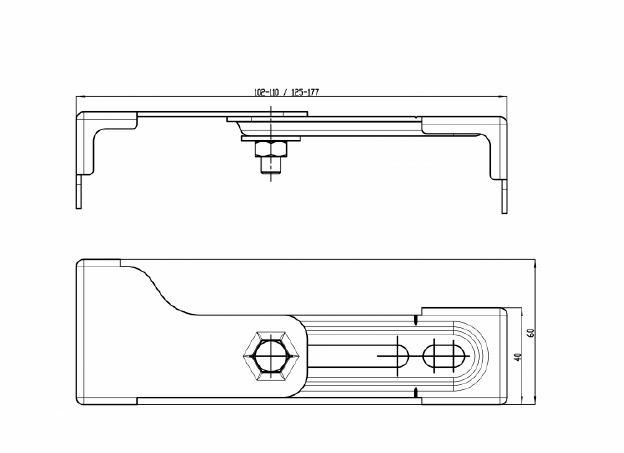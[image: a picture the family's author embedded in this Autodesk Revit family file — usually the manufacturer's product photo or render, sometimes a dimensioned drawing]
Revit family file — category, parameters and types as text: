
# Revit family: PRD_AR_PrplmbInstalFrm_InstallationFrameForToiletBowl_AQFX0006,0007
name_source: partatom
category: Plumbing Fixtures
revit_build: Autodesk Revit 2018 (Build: 20190510_1515(x64)
units: mm (PartAtom-declared; Revit-internal decimal feet)

## family parameters
Always vertical = Yes
Cut with Voids When Loaded = Yes
OmniClass Number = 23.45.00.00
OmniClass Title = Sanitary, Laundry, and Cleaning Equipment
Part Type = Normal
Room Calculation Point = No
Round Connector Dimension = Use Diameter
Shared = No
Work Plane-Based = No

## types (4) — shared parameters
Application = WC
AssetType = Fixed
Category = Pr_40_20_93_62, Pre-plumbed installation frames
Cistern = PRD_AR_PlasticMaterial
CisternCapacity = 0
CisternColor = White
CisternHeight = Other
CisternMaterial = Plastic
DurationUnit = year
Finish = powder coated
FlushRate = 0
FlushType = Push
Form = Installation frame
FrameMaterial = PRD_AR_StainlessSteel_Colored
HeightAdjustment = 200 mm  [stored 0.656168 ft]
IfcExportAs = IfcSanitaryTerminalType
IfcExportType = CISTERN
InletPipeSize = 50  [stored 0.164042 ft]
InstallationDate = 1900-12-31T23:59:59
IsAutomaticFlush = 0
IsSingleFlush = 0
Manufacturer = KWC Group AG
ManufacturerName = KWC Group AG
ManufacturerURL = www.kwc.com
Material = steel
Materials = powder coated steel
NBSDescription = Preplumbed installation frames
NBSReference = 45-35-70/421
NominalDepth = 155 mm
NominalHeight = 1120 mm  [stored 3.67454 ft]
NominalWidth = 450 mm
OverallWidth = 450 mm
ProductInformation = https://pim.kwc.com
Size = 450x1120x(135-205) mm
Type = Installation element
TypeOfMixing = no mixing
TypeOfMounting = wall and floor mounting
URL = www.kwc.com
Uniclass2015Code = Pr_40_20_93_62
Uniclass2015Title = Pre-plumbed installation frames
Uniclass2015Version = Products v1.10
Version = 1
WarrantyDurationUnit = year
WarrantyStartDate = 1900-12-31T23:59:59

## per-type parameters (varying)
| type | BIMObjectName | BarrierFree | Description | Features | GrossWeight | InletHeight | Model | ModelNumber | ModelReference | Name | NetWeight | OutletHeight | OutletPipeSize | OutletSize |
| AQFX0007 - DN100 | PRD_AR_PreplumbedInstallationFrames_InstallationFrameForToiletBowl_AQFX0007 | yes | AQUAFIX installation frame for barrier-free wall-mounted toilet bowl, with wall-installation cistern. Self-supporting, powder coated steel-frame construction, MOT tested, for individual mounting for dry-wall lining. Concealed toilet cistern with watercondensation insulation, with dual-volume flushing (7,5-4,5 l or 4-2 l) or Start/Stop flushing, triggering function transferred via flexible pressure spirals, charge valve noise group I, mounting bracket 4-fold adjustable for toilet-connecting elbow DN 90 / DN 100, complete with flexible connecting hose, toilet-connecting elbow, retaining bolts for toilet, building protection and fastening material, dimensions 450 x 1120 mm (W x H). | AQFX0007, Installation element, steel, wall and floor mounting, 450x1120x155 mm (WxHxD) | 13.10 kg | 415 mm | AQFX0007 | 2030020128 | AQFX0007 | AQUAFIX installation element for wall-mounted toilet bowl AQFX0007 | 12.45 kg | 280 mm  [stored 0.918635 ft] | 100  [stored 0.328084 ft] | 100  [stored 0.328084 ft] |
| AQFX0006 - DN100 | PRD_AR_PreplumbedInstallationFrames_InstallationFrameForToiletBowl_AQFX0006 | no | AQUAFIX installation element for wall-mounted toilet bowl, with wall-installation cistern. Self-supporting, powder coated steel-frame construction, MOT tested, for individual mounting for dry-wall lining. Concealed toilet cistern with water condensation insulation, with dual-volume flushing (7,5-4,5 l or 4-2 l) or Start/Stop flushing, triggering function transferred via flexible pressure spirals, charge valve noise group I, mounting bracket 4-fold adjustable for toilet-connecting elbow DN 90 / DN 100, complete with flexible connecting hose, toilet-connecting elbow, retaining bolts for toilet, building protection and fastening material, dimensions 450 x 1120 mm (W x H). | AQFX0006, Installation element, steel, wall and floor mounting, 450x1120x155 mm (WxHxD) | 13.50 kg | 365 mm  [stored 1.19751 ft] | AQFX0006 | 2030020126 | AQFX0006 | AQUAFIX installation element for wall-mounted toilet bowl AQFX0006 | 12.83 kg | 230 mm  [stored 0.754593 ft] | 100  [stored 0.328084 ft] | 100  [stored 0.328084 ft] |
| AQFX0006 - DN90 | PRD_AR_PreplumbedInstallationFrames_InstallationFrameForToiletBowl_AQFX0006 | no | AQUAFIX installation element for wall-mounted toilet bowl, with wall-installation cistern. Self-supporting, powder coated steel-frame construction, MOT tested, for individual mounting for dry-wall lining. Concealed toilet cistern with water condensation insulation, with dual-volume flushing (7,5-4,5 l or 4-2 l) or Start/Stop flushing, triggering function transferred via flexible pressure spirals, charge valve noise group I, mounting bracket 4-fold adjustable for toilet-connecting elbow DN 90 / DN 100, complete with flexible connecting hose, toilet-connecting elbow, retaining bolts for toilet, building protection and fastening material, dimensions 450 x 1120 mm (W x H). | AQFX0006, Installation element, steel, wall and floor mounting, 450x1120x155 mm (WxHxD) | 13.50 kg | 365 mm  [stored 1.19751 ft] | AQFX0006 | 2030020126 | AQFX0006 | AQUAFIX installation element for wall-mounted toilet bowl AQFX0006 | 12.83 kg | 230 mm  [stored 0.754593 ft] | 90 | 90 |
| AQFX0007 - DN90 | PRD_AR_PreplumbedInstallationFrames_InstallationFrameForToiletBowl_AQFX0007 | yes | AQUAFIX installation frame for barrier-free wall-mounted toilet bowl, with wall-installation cistern. Self-supporting, powder coated steel-frame construction, MOT tested, for individual mounting for dry-wall lining. Concealed toilet cistern with watercondensation insulation, with dual-volume flushing (7,5-4,5 l or 4-2 l) or Start/Stop flushing, triggering function transferred via flexible pressure spirals, charge valve noise group I, mounting bracket 4-fold adjustable for toilet-connecting elbow DN 90 / DN 100, complete with flexible connecting hose, toilet-connecting elbow, retaining bolts for toilet, building protection and fastening material, dimensions 450 x 1120 mm (W x H). | AQFX0007, Installation element, steel, wall and floor mounting, 450x1120x155 mm (WxHxD) | 13.10 kg | 415 mm | AQFX0007 | 2030020128 | AQFX0007 | AQUAFIX installation element for wall-mounted toilet bowl AQFX0007 | 12.45 kg | 280 mm  [stored 0.918635 ft] | 90 | 90 |

note: [stored X ft] marks values corroborated as IEEE doubles in the binary element streams (Revit-internal decimal feet)

## geometry (parser evidence)
native form markers: Sweep x16
no freeform markers — native parametric forms only
